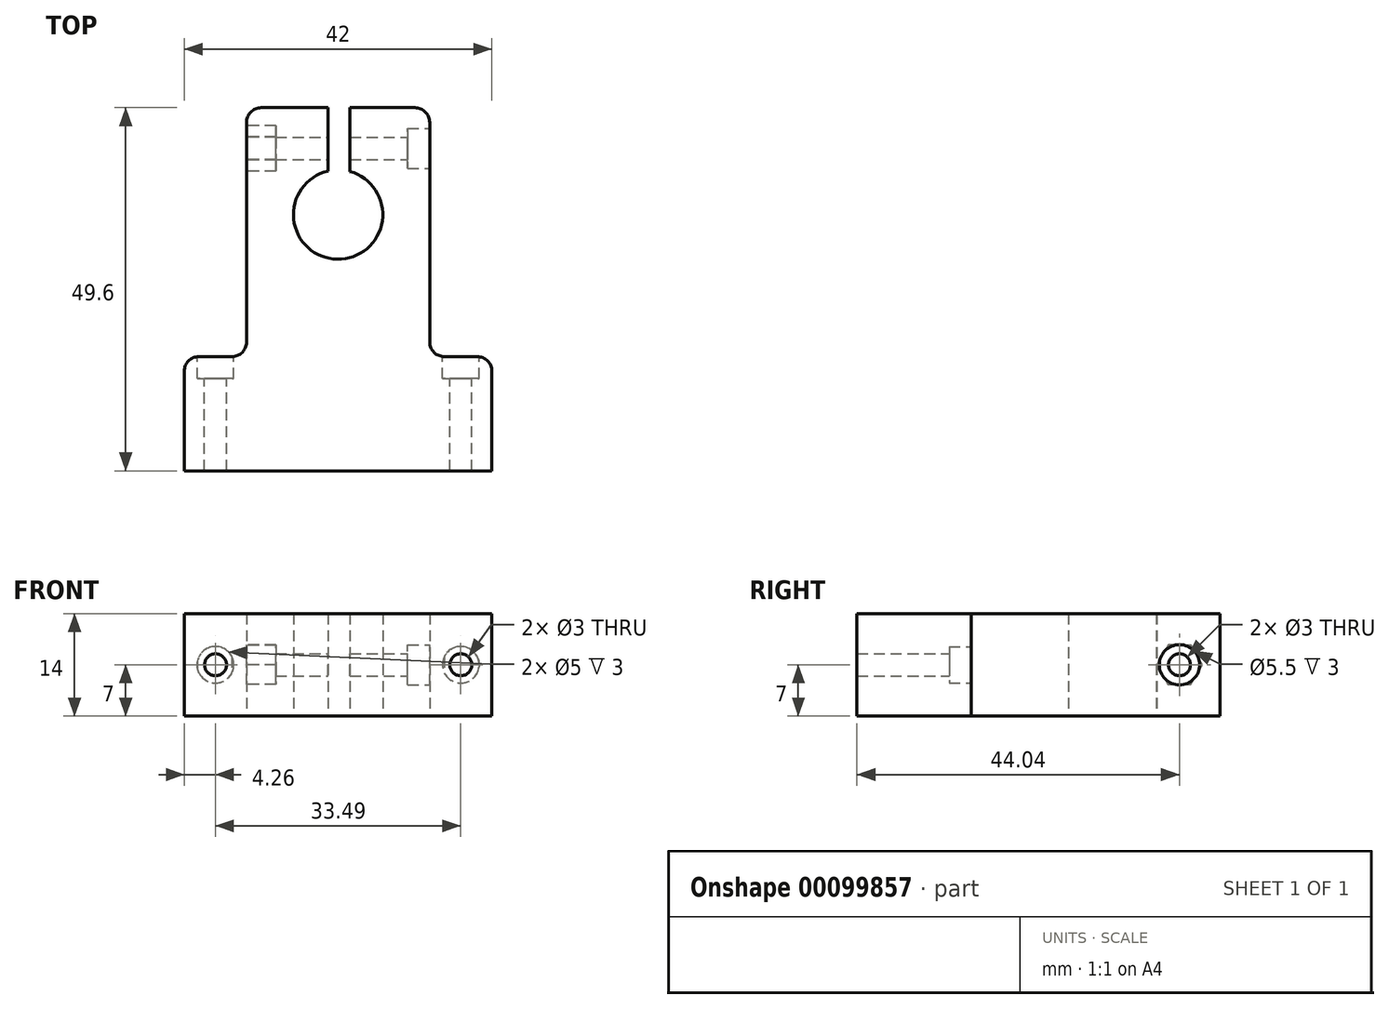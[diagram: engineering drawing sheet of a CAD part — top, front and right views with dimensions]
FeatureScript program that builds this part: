
annotation { "Feature Type Name" : "Feature", "Feature Type Description" : "" }
export const myFeature = defineFeature(function(context is Context, id is Id, definition is map)
    precondition{}
    {
        {
            var Q0;
            Q0=qCreatedBy(makeId("Top.planeOp"),FACE);
            var sketch = newSketch(context, id + "F0", { "sketchPlane" : qUnion([Q0])});
            skLineSegment(sketch, "E0", {"start": v(-72.66, -78.19) * mm, "end": v(-30.66, -78.19) * mm});
            skLineSegment(sketch, "E1", {"start": v(-30.66, -78.19) * mm, "end": v(-30.66, -64.59) * mm});
            skLineSegment(sketch, "E2", {"start": v(-32.66, -62.59) * mm, "end": v(-37.16, -62.59) * mm});
            skLineSegment(sketch, "E3", {"start": v(-39.16, -60.59) * mm, "end": v(-39.16, -30.59) * mm});
            skLineSegment(sketch, "E4", {"start": v(-41.16, -28.59) * mm, "end": v(-62.16, -28.59) * mm});
            skLineSegment(sketch, "E5", {"start": v(-64.16, -30.59) * mm, "end": v(-64.16, -60.59) * mm});
            skLineSegment(sketch, "E6", {"start": v(-66.16, -62.59) * mm, "end": v(-70.66, -62.59) * mm});
            skLineSegment(sketch, "E7", {"start": v(-72.66, -64.59) * mm, "end": v(-72.66, -78.19) * mm});
            skCircle(sketch, "E8", {"center": v(-51.66, -43.19) * mm, "radius": 6.1 * mm});
            skLineSegment(sketch, "E9", {"start": v(-51.66, -28.59) * mm, "end": v(-53.05, -28.59) * mm});
            skLineSegment(sketch, "E10.bottom", {"start": v(-53.05, -28.59) * mm, "end": v(-50.05, -28.59) * mm});
            skLineSegment(sketch, "E10.top", {"start": v(-53.05, -37.3) * mm, "end": v(-50.05, -37.3) * mm});
            skLineSegment(sketch, "E10.left", {"start": v(-53.05, -28.59) * mm, "end": v(-53.05, -37.3) * mm});
            skLineSegment(sketch, "E10.right", {"start": v(-50.05, -28.59) * mm, "end": v(-50.05, -37.3) * mm});
            skPoint(sketch, "E11.visualSharp", {"position": v(-64.16, -62.59) * mm});
            skArc(sketch, "E11.filletArc", {"start": v(-66.16, -62.59) * mm, "mid": v(-64.75, -62) * mm, "end": v(-64.16, -60.59) * mm});
            skPoint(sketch, "E12.visualSharp", {"position": v(-39.16, -62.59) * mm});
            skArc(sketch, "E12.filletArc", {"start": v(-39.16, -60.59) * mm, "mid": v(-38.57, -62) * mm, "end": v(-37.16, -62.59) * mm});
            skPoint(sketch, "E13.visualSharp", {"position": v(-64.16, -28.59) * mm});
            skArc(sketch, "E13.filletArc", {"start": v(-62.16, -28.59) * mm, "mid": v(-63.57, -29.18) * mm, "end": v(-64.16, -30.59) * mm});
            skPoint(sketch, "E14.visualSharp", {"position": v(-39.16, -28.59) * mm});
            skArc(sketch, "E14.filletArc", {"start": v(-39.16, -30.59) * mm, "mid": v(-39.75, -29.18) * mm, "end": v(-41.16, -28.59) * mm});
            skPoint(sketch, "E15.visualSharp", {"position": v(-72.66, -62.59) * mm});
            skArc(sketch, "E15.filletArc", {"start": v(-70.66, -62.59) * mm, "mid": v(-72.07, -63.18) * mm, "end": v(-72.66, -64.59) * mm});
            skPoint(sketch, "E16.visualSharp", {"position": v(-30.66, -62.59) * mm});
            skArc(sketch, "E16.filletArc", {"start": v(-30.66, -64.59) * mm, "mid": v(-31.25, -63.18) * mm, "end": v(-32.66, -62.59) * mm});
            skSolve(sketch);
        }
        {
            var Q0;
            Q0=makeQuery(id+"F0.imprint","IMPRINT",FACE,{"disambiguationData":[TD([[makeQuery(id+"F0.imprint","IMPRINT",EDGE,{"derivedFrom":sQuery(id+"F0.wireOp",EDGE,"E0")}),1.0]])]});
            extrude(context, id + "F1", {"entities" : qUnion([Q0]), "depth" : 14 * mm});
        }
        {
            var Q0;
            Q0=makeQuery(id+"F1.opExtrude","SWEPT_FACE",FACE,{"disambiguationData":[OSD([sQuery(id+"F0.wireOp",EDGE,"E3")])]});
            var sketch = newSketch(context, id + "F2", { "sketchPlane" : qUnion([Q0])});
            skCircle(sketch, "E17", {"center": v(-34.15, 7) * mm, "radius": 1.5 * mm});
            skPoint(sketch, "E17.centerSnap0", {"position": v(-30.59, 7) * mm});
            skSolve(sketch);
        }
        {
            var Q0;
            Q0=sQuery(id+"F2.wireOp",VERTEX,"E17.center");
            var Q1;
            Q1=makeQuery(id+"F1.opExtrude","SWEPT_BODY",BODY,{"disambiguationData":[OSD([sQuery(id+"F0.wireOp",EDGE,"E0"),sQuery(id+"F0.wireOp",EDGE,"E1"),sQuery(id+"F0.wireOp",EDGE,"E2"),sQuery(id+"F0.wireOp",EDGE,"E3"),sQuery(id+"F0.wireOp",EDGE,"E4"),sQuery(id+"F0.wireOp",EDGE,"E5"),sQuery(id+"F0.wireOp",EDGE,"E6"),sQuery(id+"F0.wireOp",EDGE,"E7"),sQuery(id+"F0.wireOp",EDGE,"E8"),sQuery(id+"F0.wireOp",EDGE,"E10.left"),sQuery(id+"F0.wireOp",EDGE,"E10.right"),sQuery(id+"F0.wireOp",EDGE,"E11.filletArc"),sQuery(id+"F0.wireOp",EDGE,"E12.filletArc"),sQuery(id+"F0.wireOp",EDGE,"E13.filletArc"),sQuery(id+"F0.wireOp",EDGE,"E14.filletArc"),sQuery(id+"F0.wireOp",EDGE,"E15.filletArc"),sQuery(id+"F0.wireOp",EDGE,"E16.filletArc")])]});
            hole(context, id + "F3", {"style" : HoleStyle.C_BORE, "endStyle" : HoleEndStyle.THROUGH, "holeDiameter" : 3 * mm, "cBoreDiameter" : 5.5 * mm, "cBoreDepth" : 3 * mm, "locations" : qUnion([Q0]), "scope" : qUnion([Q1]), "isTappedThrough" : true});
        }
        {
            var Q0;
            Q0=makeQuery(id+"F1.opExtrude","SWEPT_FACE",FACE,{"disambiguationData":[OSD([sQuery(id+"F0.wireOp",EDGE,"E2")])]});
            var sketch = newSketch(context, id + "F4", { "sketchPlane" : qUnion([Q0])});
            skCircle(sketch, "E18", {"center": v(34.91, 7) * mm, "radius": 1.75 * mm});
            skPoint(sketch, "E18.centerSnap0", {"position": v(32.66, 7) * mm});
            skPoint(sketch, "E18.centerSnap1", {"position": v(34.91, 14) * mm});
            skCircle(sketch, "E19", {"center": v(68.4, 7) * mm, "radius": 1.75 * mm});
            skSolve(sketch);
        }
        {
            var Q0;
            Q0=sQuery(id+"F4.wireOp",VERTEX,"E19.center");
            var Q1;
            Q1=sQuery(id+"F4.wireOp",VERTEX,"E18.center");
            var Q2;
            Q2=makeQuery(id+"F1.opExtrude","SWEPT_BODY",BODY,{"disambiguationData":[OSD([sQuery(id+"F0.wireOp",EDGE,"E0"),sQuery(id+"F0.wireOp",EDGE,"E1"),sQuery(id+"F0.wireOp",EDGE,"E2"),sQuery(id+"F0.wireOp",EDGE,"E3"),sQuery(id+"F0.wireOp",EDGE,"E4"),sQuery(id+"F0.wireOp",EDGE,"E5"),sQuery(id+"F0.wireOp",EDGE,"E6"),sQuery(id+"F0.wireOp",EDGE,"E7"),sQuery(id+"F0.wireOp",EDGE,"E8"),sQuery(id+"F0.wireOp",EDGE,"E10.left"),sQuery(id+"F0.wireOp",EDGE,"E10.right"),sQuery(id+"F0.wireOp",EDGE,"E11.filletArc"),sQuery(id+"F0.wireOp",EDGE,"E12.filletArc"),sQuery(id+"F0.wireOp",EDGE,"E13.filletArc"),sQuery(id+"F0.wireOp",EDGE,"E14.filletArc"),sQuery(id+"F0.wireOp",EDGE,"E15.filletArc"),sQuery(id+"F0.wireOp",EDGE,"E16.filletArc")])]});
            hole(context, id + "F5", {"style" : HoleStyle.C_BORE, "endStyle" : HoleEndStyle.THROUGH, "holeDiameter" : 3 * mm, "cBoreDiameter" : 5 * mm, "cBoreDepth" : 3 * mm, "locations" : qUnion([Q0, Q1]), "scope" : qUnion([Q2]), "isTappedThrough" : true});
        }
        {
            var Q0;
            Q0=makeQuery(id+"F1.opExtrude","SWEPT_FACE",FACE,{"disambiguationData":[OSD([sQuery(id+"F0.wireOp",EDGE,"E5")])]});
            var sketch = newSketch(context, id + "F6", { "sketchPlane" : qUnion([Q0])});
            skCircle(sketch, "E20.cCircle", {"center": v(34.15, 7) * mm, "radius": 2.7 * mm, "construction": true});
            skLineSegment(sketch, "E20.0", {"start": v(37.26, 7.02) * mm, "end": v(35.72, 4.32) * mm});
            skLineSegment(sketch, "E20.1", {"start": v(35.72, 4.32) * mm, "end": v(32.61, 4.3) * mm});
            skLineSegment(sketch, "E20.2", {"start": v(32.61, 4.3) * mm, "end": v(31.04, 6.98) * mm});
            skLineSegment(sketch, "E20.3", {"start": v(31.04, 6.98) * mm, "end": v(32.58, 9.68) * mm});
            skLineSegment(sketch, "E20.4", {"start": v(32.58, 9.68) * mm, "end": v(35.69, 9.7) * mm});
            skLineSegment(sketch, "E20.5", {"start": v(35.69, 9.7) * mm, "end": v(37.26, 7.02) * mm});
            skPoint(sketch, "E20.0.midPoint", {"position": v(36.49, 5.67) * mm});
            skSolve(sketch);
        }
        {
            var Q0;
            Q0=makeQuery(id+"F6.imprint","IMPRINT",FACE,{"disambiguationData":[TD([[makeQuery(id+"F6.imprint","IMPRINT",EDGE,{"derivedFrom":sQuery(id+"F6.wireOp",EDGE,"E20.0")}),-1.0]])]});
            extrude(context, id + "F7", {"entities" : qUnion([Q0]), "operationType" : NewBodyOperationType.REMOVE, "oppositeDirection" : true, "depth" : 4 * mm});
        }
    });
